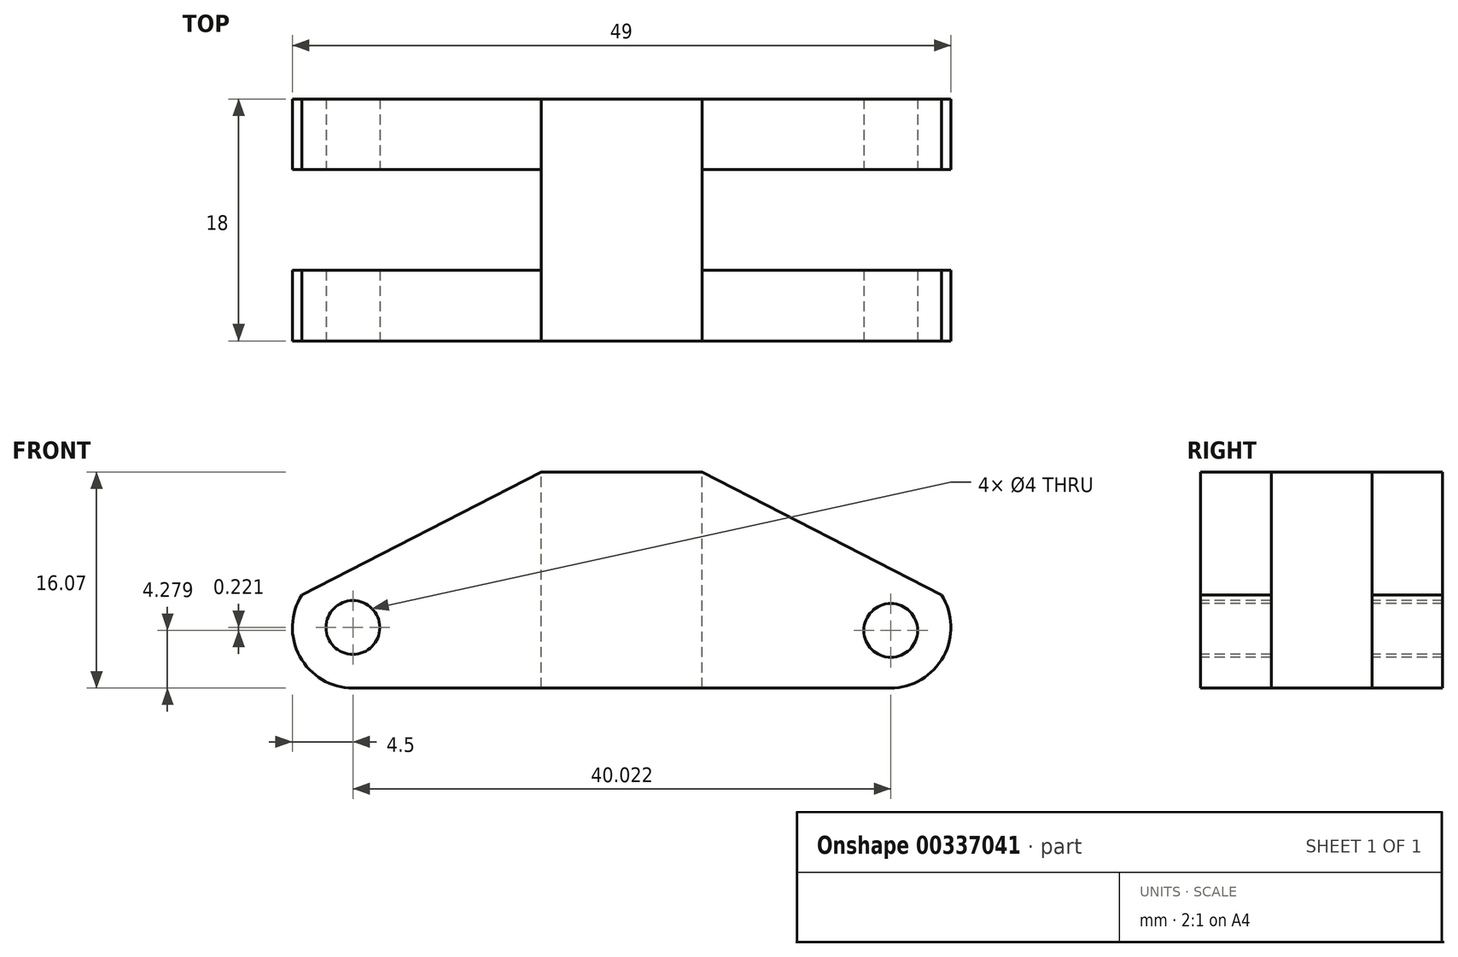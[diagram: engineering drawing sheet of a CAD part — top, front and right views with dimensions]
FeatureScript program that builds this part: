
annotation { "Feature Type Name" : "Feature", "Feature Type Description" : "" }
export const myFeature = defineFeature(function(context is Context, id is Id, definition is map)
    precondition{}
    {
        {
            var Q0;
            Q0=qCreatedBy(makeId("Front.planeOp"),FACE);
            var sketch = newSketch(context, id + "F0", { "sketchPlane" : qUnion([Q0])});
            skLineSegment(sketch, "E0", {"start": v(0, 0) * mm, "end": v(-20, 0) * mm});
            skLineSegment(sketch, "E1", {"start": v(0, 0) * mm, "end": v(20, 0) * mm});
            skArc(sketch, "E2", {"start": v(-20, 0) * mm, "mid": v(-23.95, 2.34) * mm, "end": v(-23.79, 6.93) * mm});
            skArc(sketch, "E3", {"start": v(20, 0) * mm, "mid": v(23.95, 2.34) * mm, "end": v(23.79, 6.93) * mm});
            skLineSegment(sketch, "E4", {"start": v(-23.79, 6.93) * mm, "end": v(-6, 16.07) * mm});
            skLineSegment(sketch, "E5", {"start": v(23.79, 6.93) * mm, "end": v(6, 16.07) * mm});
            skLineSegment(sketch, "E6", {"start": v(-6, 16.07) * mm, "end": v(6, 16.07) * mm});
            skSolve(sketch);
        }
        {
            var Q0;
            Q0=makeQuery(id+"F0.imprint","IMPRINT",FACE,{"disambiguationData":[TD([[makeQuery(id+"F0.imprint","IMPRINT",EDGE,{"derivedFrom":sQuery(id+"F0.wireOp",EDGE,"E0")}),-1.0]])]});
            extrude(context, id + "F1", {"entities" : qUnion([Q0]), "depth" : 18 * mm});
        }
        {
            var Q0;
            Q0=makeQuery(id+"F1.opExtrude","SWEPT_FACE",FACE,{"disambiguationData":[OSD([sQuery(id+"F0.wireOp",EDGE,"E6")])]});
            var sketch = newSketch(context, id + "F2", { "sketchPlane" : qUnion([Q0])});
            skLineSegment(sketch, "E7", {"start": v(0, 0) * mm, "end": v(0, -18) * mm, "construction": true});
            skLineSegment(sketch, "E8", {"start": v(-6, -9) * mm, "end": v(6, -9) * mm, "construction": true});
            skLineSegment(sketch, "E9.bottom", {"start": v(-37.43, -5.25) * mm, "end": v(37.43, -5.25) * mm});
            skLineSegment(sketch, "E9.top", {"start": v(-37.43, -12.75) * mm, "end": v(37.43, -12.75) * mm});
            skLineSegment(sketch, "E9.left", {"start": v(-37.43, -5.25) * mm, "end": v(-37.43, -12.75) * mm});
            skLineSegment(sketch, "E9.right", {"start": v(37.43, -5.25) * mm, "end": v(37.43, -12.75) * mm});
            skPoint(sketch, "E9.middle", {"position": v(0, -9) * mm});
            skSolve(sketch);
        }
        {
            var Q0;
            {var subQ0=sQuery(id+"F2.wireOp",EDGE,"E9.left");Q0=makeQuery(id+"F2.imprint","IMPRINT",FACE,{"disambiguationData":[TD([[makeQuery(id+"F2.imprint","IMPRINT",EDGE,{"derivedFrom":subQ0}),1.0]])]});}
            var Q1;
            {var subQ0=sQuery(id+"F2.wireOp",EDGE,"E9.right");Q1=makeQuery(id+"F2.imprint","IMPRINT",FACE,{"disambiguationData":[TD([[makeQuery(id+"F2.imprint","IMPRINT",EDGE,{"derivedFrom":subQ0}),-1.0]])]});}
            extrude(context, id + "F3", {"entities" : qUnion([Q0, Q1]), "operationType" : NewBodyOperationType.REMOVE, "oppositeDirection" : true, "depth" : 25 * mm});
        }
        {
            var Q0;
            Q0=makeQuery(id+"F1.opExtrude","CAP_FACE",FACE,{"disambiguationData":[OSD([sQuery(id+"F0.wireOp",EDGE,"E0"),sQuery(id+"F0.wireOp",EDGE,"E1"),sQuery(id+"F0.wireOp",EDGE,"E2"),sQuery(id+"F0.wireOp",EDGE,"E3"),sQuery(id+"F0.wireOp",EDGE,"E4"),sQuery(id+"F0.wireOp",EDGE,"E5"),sQuery(id+"F0.wireOp",EDGE,"E6")])],"isStart":false});
            var sketch = newSketch(context, id + "F4", { "sketchPlane" : qUnion([Q0])});
            skCircle(sketch, "E10", {"center": v(-20, 4.5) * mm, "radius": 2 * mm});
            skCircle(sketch, "E11", {"center": v(20.02, 4.28) * mm, "radius": 2 * mm});
            skSolve(sketch);
        }
        {
            var Q0;
            Q0=makeQuery(id+"F4.imprint","IMPRINT",FACE,{"disambiguationData":[TD([[makeQuery(id+"F4.imprint","IMPRINT",EDGE,{"derivedFrom":sQuery(id+"F4.wireOp",EDGE,"E10")}),1.0]])]});
            var Q1;
            Q1=makeQuery(id+"F4.imprint","IMPRINT",FACE,{"disambiguationData":[TD([[makeQuery(id+"F4.imprint","IMPRINT",EDGE,{"derivedFrom":sQuery(id+"F4.wireOp",EDGE,"E11")}),1.0]])]});
            extrude(context, id + "F5", {"entities" : qUnion([Q0, Q1]), "operationType" : NewBodyOperationType.REMOVE, "oppositeDirection" : true, "depth" : 25 * mm});
        }
    });
